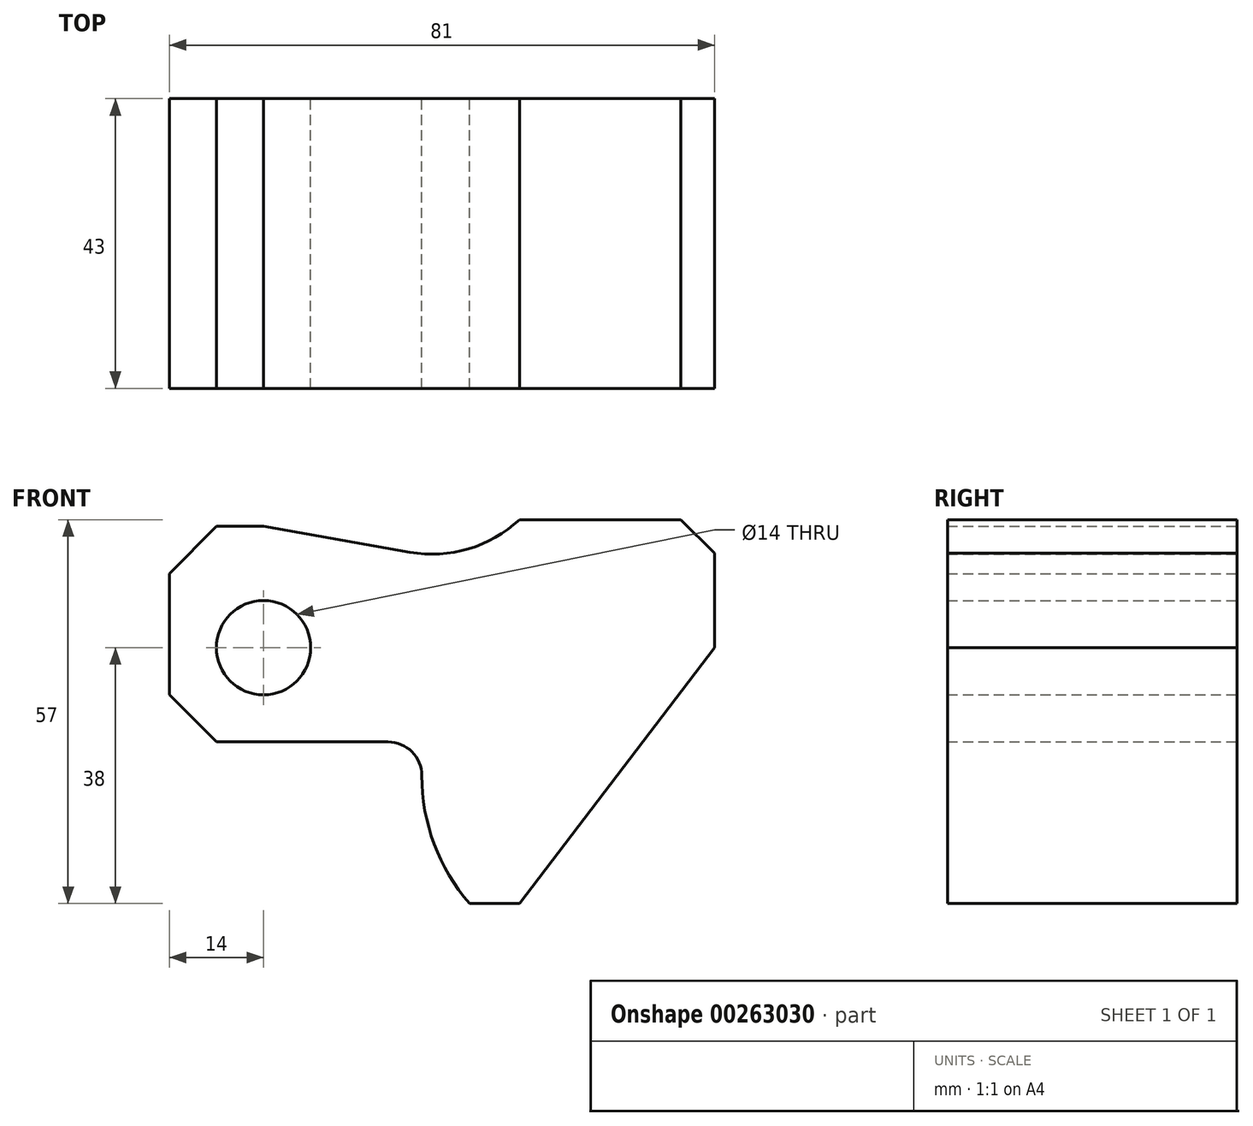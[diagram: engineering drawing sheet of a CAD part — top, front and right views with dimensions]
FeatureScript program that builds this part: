
annotation { "Feature Type Name" : "Feature", "Feature Type Description" : "" }
export const myFeature = defineFeature(function(context is Context, id is Id, definition is map)
    precondition{}
    {
        {
            var Q0;
            Q0=qCreatedBy(makeId("Front.planeOp"),FACE);
            var sketch = newSketch(context, id + "F0", { "sketchPlane" : qUnion([Q0])});
            skCircle(sketch, "E0", {"center": v(0, 0) * mm, "radius": 7 * mm});
            skLineSegment(sketch, "E1", {"start": v(67, 0) * mm, "end": v(67, 14) * mm});
            skLineSegment(sketch, "E2", {"start": v(-14, -7) * mm, "end": v(-14, 11) * mm});
            skLineSegment(sketch, "E3", {"start": v(-14, 11) * mm, "end": v(-7, 18) * mm});
            skLineSegment(sketch, "E4", {"start": v(-7, 18) * mm, "end": v(0, 18) * mm});
            skLineSegment(sketch, "E5", {"start": v(-14, -7) * mm, "end": v(-7, -14) * mm});
            skLineSegment(sketch, "E6", {"start": v(-7, -14) * mm, "end": v(18.5, -14) * mm});
            skArc(sketch, "E7", {"start": v(23.5, -19) * mm, "mid": v(22.04, -15.46) * mm, "end": v(18.5, -14) * mm});
            skLineSegment(sketch, "E8", {"start": v(38, 19) * mm, "end": v(62, 19) * mm});
            skLineSegment(sketch, "E9", {"start": v(62, 19) * mm, "end": v(67, 14) * mm});
            skLineSegment(sketch, "E10", {"start": v(38, -38) * mm, "end": v(30.6, -38) * mm});
            skArc(sketch, "E11", {"start": v(23.5, -19) * mm, "mid": v(25.33, -29.14) * mm, "end": v(30.6, -38) * mm});
            skLineSegment(sketch, "E12", {"start": v(0, 18) * mm, "end": v(21.73, 14.17) * mm});
            skArc(sketch, "E13", {"start": v(21.73, 14.17) * mm, "mid": v(30.43, 14.67) * mm, "end": v(38, 19) * mm});
            skLineSegment(sketch, "E14", {"start": v(0, 18) * mm, "end": v(18.32, 18) * mm, "construction": true});
            skLineSegment(sketch, "E15", {"start": v(38, -38) * mm, "end": v(67, 0) * mm});
            skSolve(sketch);
        }
        {
            var Q0;
            Q0=makeQuery(id+"F0.imprint","IMPRINT",FACE,{"disambiguationData":[TD([[makeQuery(id+"F0.imprint","IMPRINT",EDGE,{"derivedFrom":sQuery(id+"F0.wireOp",EDGE,"E0")}),-1.0]])]});
            extrude(context, id + "F1", {"entities" : qUnion([Q0]), "depth" : 43 * mm});
        }
    });
